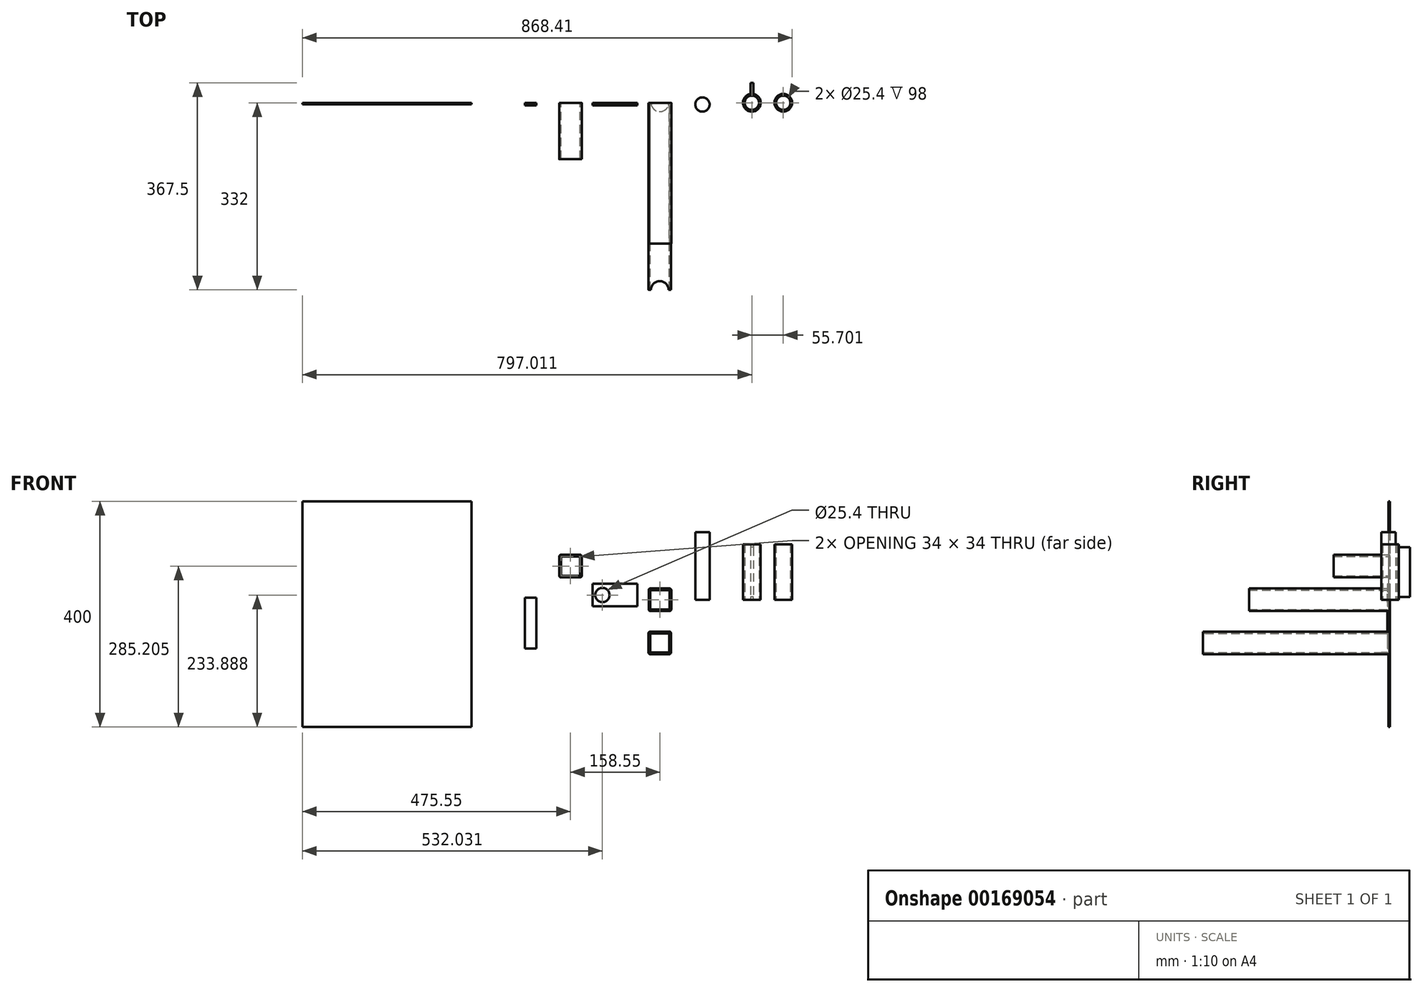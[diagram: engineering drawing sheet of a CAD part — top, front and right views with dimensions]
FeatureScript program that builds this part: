
annotation { "Feature Type Name" : "Feature", "Feature Type Description" : "" }
export const myFeature = defineFeature(function(context is Context, id is Id, definition is map)
    precondition{}
    {
        {
            var Q0;
            Q0=qCreatedBy(makeId("Front.planeOp"),FACE);
            var sketch = newSketch(context, id + "F0", { "sketchPlane" : qUnion([Q0])});
            skLineSegment(sketch, "E0.bottom", {"start": v(17, 20) * mm, "end": v(-17, 20) * mm});
            skLineSegment(sketch, "E0.top", {"start": v(17, -20) * mm, "end": v(-17, -20) * mm});
            skLineSegment(sketch, "E0.left", {"start": v(20, 17) * mm, "end": v(20, -17) * mm});
            skLineSegment(sketch, "E0.right", {"start": v(-20, 17) * mm, "end": v(-20, -17) * mm});
            skPoint(sketch, "E0.middle", {"position": v(0, 0) * mm});
            skLineSegment(sketch, "E1.0", {"start": v(15, 17) * mm, "end": v(-15, 17) * mm});
            skLineSegment(sketch, "E1.1", {"start": v(17, 15) * mm, "end": v(17, -15) * mm});
            skLineSegment(sketch, "E1.2", {"start": v(15, -17) * mm, "end": v(-15, -17) * mm});
            skLineSegment(sketch, "E1.3", {"start": v(-17, 15) * mm, "end": v(-17, -15) * mm});
            skPoint(sketch, "E2.visualSharp", {"position": v(-20, 20) * mm});
            skArc(sketch, "E2.filletArc", {"start": v(-17, 20) * mm, "mid": v(-19.12, 19.12) * mm, "end": v(-20, 17) * mm});
            skPoint(sketch, "E3.visualSharp", {"position": v(20, 20) * mm});
            skArc(sketch, "E3.filletArc", {"start": v(20, 17) * mm, "mid": v(19.12, 19.12) * mm, "end": v(17, 20) * mm});
            skPoint(sketch, "E4.visualSharp", {"position": v(20, -20) * mm});
            skArc(sketch, "E4.filletArc", {"start": v(17, -20) * mm, "mid": v(19.12, -19.12) * mm, "end": v(20, -17) * mm});
            skPoint(sketch, "E5.visualSharp", {"position": v(-20, -20) * mm});
            skArc(sketch, "E5.filletArc", {"start": v(-20, -17) * mm, "mid": v(-19.12, -19.12) * mm, "end": v(-17, -20) * mm});
            skArc(sketch, "E6.filletArc", {"start": v(15, -17) * mm, "mid": v(16.41, -16.41) * mm, "end": v(17, -15) * mm});
            skArc(sketch, "E7.filletArc", {"start": v(17, 15) * mm, "mid": v(16.41, 16.41) * mm, "end": v(15, 17) * mm});
            skArc(sketch, "E8.filletArc", {"start": v(-15, 17) * mm, "mid": v(-16.41, 16.41) * mm, "end": v(-17, 15) * mm});
            skArc(sketch, "E9.filletArc", {"start": v(-17, -15) * mm, "mid": v(-16.41, -16.41) * mm, "end": v(-15, -17) * mm});
            skSolve(sketch);
        }
        {
            var Q0;
            Q0=makeQuery(id+"F0.imprint","IMPRINT",FACE,{"disambiguationData":[TD([[makeQuery(id+"F0.imprint","IMPRINT",EDGE,{"derivedFrom":sQuery(id+"F0.wireOp",EDGE,"E0.bottom")}),1.0]])]});
            extrude(context, id + "F1", {"entities" : qUnion([Q0]), "depth" : 250 * mm});
        }
        {
            var Q0;
            Q0=qCreatedBy(makeId("Front.planeOp"),FACE);
            var sketch = newSketch(context, id + "F2", { "sketchPlane" : qUnion([Q0])});
            skLineSegment(sketch, "E10.bottom", {"start": v(-141.55, 79.68) * mm, "end": v(-175.55, 79.68) * mm});
            skLineSegment(sketch, "E10.top", {"start": v(-141.55, 39.68) * mm, "end": v(-175.55, 39.68) * mm});
            skLineSegment(sketch, "E10.left", {"start": v(-138.55, 76.68) * mm, "end": v(-138.55, 42.68) * mm});
            skLineSegment(sketch, "E10.right", {"start": v(-178.55, 76.68) * mm, "end": v(-178.55, 42.68) * mm});
            skPoint(sketch, "E10.middle", {"position": v(-158.55, 59.68) * mm});
            skLineSegment(sketch, "E11.0", {"start": v(-143.55, 76.68) * mm, "end": v(-173.55, 76.68) * mm});
            skLineSegment(sketch, "E11.1", {"start": v(-141.55, 74.68) * mm, "end": v(-141.55, 44.68) * mm});
            skLineSegment(sketch, "E11.2", {"start": v(-143.55, 42.68) * mm, "end": v(-173.55, 42.68) * mm});
            skLineSegment(sketch, "E11.3", {"start": v(-175.55, 74.68) * mm, "end": v(-175.55, 44.68) * mm});
            skPoint(sketch, "E12.visualSharp", {"position": v(-178.55, 79.68) * mm});
            skArc(sketch, "E12.filletArc", {"start": v(-175.55, 79.68) * mm, "mid": v(-177.67, 78.8) * mm, "end": v(-178.55, 76.68) * mm});
            skPoint(sketch, "E13.visualSharp", {"position": v(-138.55, 79.68) * mm});
            skArc(sketch, "E13.filletArc", {"start": v(-138.55, 76.68) * mm, "mid": v(-139.43, 78.8) * mm, "end": v(-141.55, 79.68) * mm});
            skPoint(sketch, "E14.visualSharp", {"position": v(-138.55, 39.68) * mm});
            skArc(sketch, "E14.filletArc", {"start": v(-141.55, 39.68) * mm, "mid": v(-139.43, 40.56) * mm, "end": v(-138.55, 42.68) * mm});
            skPoint(sketch, "E15.visualSharp", {"position": v(-178.55, 39.68) * mm});
            skArc(sketch, "E15.filletArc", {"start": v(-178.55, 42.68) * mm, "mid": v(-177.67, 40.56) * mm, "end": v(-175.55, 39.68) * mm});
            skArc(sketch, "E16.filletArc", {"start": v(-143.55, 42.68) * mm, "mid": v(-142.14, 43.27) * mm, "end": v(-141.55, 44.68) * mm});
            skArc(sketch, "E17.filletArc", {"start": v(-141.55, 74.68) * mm, "mid": v(-142.14, 76.1) * mm, "end": v(-143.55, 76.68) * mm});
            skArc(sketch, "E18.filletArc", {"start": v(-173.55, 76.68) * mm, "mid": v(-174.96, 76.1) * mm, "end": v(-175.55, 74.68) * mm});
            skArc(sketch, "E19.filletArc", {"start": v(-175.55, 44.68) * mm, "mid": v(-174.96, 43.27) * mm, "end": v(-173.55, 42.68) * mm});
            skSolve(sketch);
        }
        {
            var Q0;
            Q0=makeQuery(id+"F2.imprint","IMPRINT",FACE,{"disambiguationData":[TD([[makeQuery(id+"F2.imprint","IMPRINT",EDGE,{"derivedFrom":sQuery(id+"F2.wireOp",EDGE,"E10.bottom")}),1.0]])]});
            extrude(context, id + "F3", {"entities" : qUnion([Q0]), "depth" : 100 * mm});
        }
        {
            var Q0;
            Q0=qCreatedBy(makeId("Front.planeOp"),FACE);
            var sketch = newSketch(context, id + "F4", { "sketchPlane" : qUnion([Q0])});
            skLineSegment(sketch, "E20.bottom", {"start": v(-119.77, 28.37) * mm, "end": v(-39.77, 28.37) * mm});
            skLineSegment(sketch, "E20.top", {"start": v(-119.77, -11.63) * mm, "end": v(-39.77, -11.63) * mm});
            skLineSegment(sketch, "E20.left", {"start": v(-119.77, 28.37) * mm, "end": v(-119.77, -11.63) * mm});
            skLineSegment(sketch, "E20.right", {"start": v(-39.77, 28.37) * mm, "end": v(-39.77, -11.63) * mm});
            skCircle(sketch, "E21", {"center": v(-102.07, 8.37) * mm, "radius": 12.7 * mm});
            skPoint(sketch, "E21.centerSnap0", {"position": v(-119.77, 8.37) * mm});
            skSolve(sketch);
        }
        {
            var Q0;
            Q0=makeQuery(id+"F4.imprint","IMPRINT",FACE,{"disambiguationData":[TD([[makeQuery(id+"F4.imprint","IMPRINT",EDGE,{"derivedFrom":sQuery(id+"F4.wireOp",EDGE,"E20.bottom")}),-1.0]])]});
            extrude(context, id + "F5", {"entities" : qUnion([Q0]), "depth" : 5 * mm});
        }
        {
            var Q0;
            Q0=qCreatedBy(makeId("Top.planeOp"),FACE);
            var sketch = newSketch(context, id + "F6", { "sketchPlane" : qUnion([Q0])});
            skCircle(sketch, "E22", {"center": v(75.3, -3.08) * mm, "radius": 12.7 * mm});
            skSolve(sketch);
        }
        {
            var Q0;
            Q0 = qSketchRegion(id + "F6", true);
            extrude(context, id + "F7", {"entities" : qUnion([Q0]), "depth" : 120 * mm});
        }
        {
            var Q0;
            Q0=qCreatedBy(makeId("Top.planeOp"),FACE);
            var sketch = newSketch(context, id + "F8", { "sketchPlane" : qUnion([Q0])});
            skCircle(sketch, "E23", {"center": v(162.91, 0) * mm, "radius": 12.7 * mm});
            skCircle(sketch, "E24.0", {"center": v(162.91, 0) * mm, "radius": 15.7 * mm});
            skLineSegment(sketch, "E25", {"start": v(160.41, 15.5) * mm, "end": v(160.41, 35.5) * mm});
            skLineSegment(sketch, "E26", {"start": v(160.41, 35.5) * mm, "end": v(165.41, 35.5) * mm});
            skLineSegment(sketch, "E27", {"start": v(165.41, 35.5) * mm, "end": v(165.41, 15.5) * mm});
            skPoint(sketch, "E28", {"position": v(162.91, 35.5) * mm});
            skSolve(sketch);
        }
        {
            var Q0;
            Q0 = qSketchRegion(id + "F8", true);
            extrude(context, id + "F9", {"entities" : qUnion([Q0]), "depth" : 98 * mm});
        }
        {
            var Q0;
            Q0=qCreatedBy(makeId("Front.planeOp"),FACE);
            var sketch = newSketch(context, id + "F10", { "sketchPlane" : qUnion([Q0])});
            skLineSegment(sketch, "E29.bottom", {"start": v(-239.33, 3.6) * mm, "end": v(-219.33, 3.6) * mm});
            skLineSegment(sketch, "E29.top", {"start": v(-239.33, -86.4) * mm, "end": v(-219.33, -86.4) * mm});
            skLineSegment(sketch, "E29.left", {"start": v(-239.33, 3.6) * mm, "end": v(-239.33, -86.4) * mm});
            skLineSegment(sketch, "E29.right", {"start": v(-219.33, 3.6) * mm, "end": v(-219.33, -86.4) * mm});
            skSolve(sketch);
        }
        {
            var Q0;
            Q0=makeQuery(id+"F10.imprint","IMPRINT",FACE,{"disambiguationData":[TD([[makeQuery(id+"F10.imprint","IMPRINT",EDGE,{"derivedFrom":sQuery(id+"F10.wireOp",EDGE,"E29.bottom")}),-1.0]])]});
            extrude(context, id + "F11", {"entities" : qUnion([Q0]), "depth" : 5 * mm});
        }
        {
            var Q0;
            Q0=qCreatedBy(makeId("Front.planeOp"),FACE);
            var sketch = newSketch(context, id + "F12", { "sketchPlane" : qUnion([Q0])});
            skLineSegment(sketch, "E30.bottom", {"start": v(-634.1, 174.48) * mm, "end": v(-334.1, 174.48) * mm});
            skLineSegment(sketch, "E30.top", {"start": v(-634.1, -225.52) * mm, "end": v(-334.1, -225.52) * mm});
            skLineSegment(sketch, "E30.left", {"start": v(-634.1, 174.48) * mm, "end": v(-634.1, -225.52) * mm});
            skLineSegment(sketch, "E30.right", {"start": v(-334.1, 174.48) * mm, "end": v(-334.1, -225.52) * mm});
            skSolve(sketch);
        }
        {
            var Q0;
            Q0=makeQuery(id+"F12.imprint","IMPRINT",FACE,{"disambiguationData":[TD([[makeQuery(id+"F12.imprint","IMPRINT",EDGE,{"derivedFrom":sQuery(id+"F12.wireOp",EDGE,"E30.bottom")}),-1.0]])]});
            extrude(context, id + "F13", {"entities" : qUnion([Q0]), "depth" : 3 * mm});
        }
        {
            var Q0;
            Q0=makeQuery(id+"F9.opExtrude","SWEPT_FACE",FACE,{"disambiguationData":[OSD([sQuery(id+"F8.wireOp",EDGE,"E25")])]});
            var sketch = newSketch(context, id + "F14", { "sketchPlane" : qUnion([Q0])});
            skLineSegment(sketch, "E31.bottom", {"start": v(-35.5, 0) * mm, "end": v(-15.5, 0) * mm});
            skLineSegment(sketch, "E31.top", {"start": v(-35.5, 5) * mm, "end": v(-15.5, 5) * mm});
            skLineSegment(sketch, "E31.left", {"start": v(-35.5, 0) * mm, "end": v(-35.5, 5) * mm});
            skLineSegment(sketch, "E31.right", {"start": v(-15.5, 0) * mm, "end": v(-15.5, 5) * mm});
            skLineSegment(sketch, "E32.bottom", {"start": v(-35.5, 98) * mm, "end": v(-15.5, 98) * mm});
            skLineSegment(sketch, "E32.top", {"start": v(-35.5, 93) * mm, "end": v(-15.5, 93) * mm});
            skLineSegment(sketch, "E32.left", {"start": v(-35.5, 98) * mm, "end": v(-35.5, 93) * mm});
            skLineSegment(sketch, "E32.right", {"start": v(-15.5, 98) * mm, "end": v(-15.5, 93) * mm});
            skSolve(sketch);
        }
        {
            var Q0;
            Q0 = qSketchRegion(id + "F14", true);
            extrude(context, id + "F15", {"entities" : qUnion([Q0]), "operationType" : NewBodyOperationType.REMOVE, "oppositeDirection" : true, "depth" : 25 * mm});
        }
        {
            var Q0;
            Q0=qCreatedBy(makeId("Top.planeOp"),FACE);
            var sketch = newSketch(context, id + "F16", { "sketchPlane" : qUnion([Q0])});
            skCircle(sketch, "E33", {"center": v(218.61, 0) * mm, "radius": 12.7 * mm});
            skCircle(sketch, "E34.0", {"center": v(218.61, 0) * mm, "radius": 15.7 * mm});
            skSolve(sketch);
        }
        {
            var Q0;
            Q0=makeQuery(id+"F16.imprint","IMPRINT",FACE,{"disambiguationData":[TD([[makeQuery(id+"F16.imprint","IMPRINT",EDGE,{"derivedFrom":sQuery(id+"F16.wireOp",EDGE,"E33")}),-1.0]])]});
            extrude(context, id + "F17", {"entities" : qUnion([Q0]), "depth" : 98 * mm});
        }
        {
            var Q0;
            Q0=qCreatedBy(makeId("Front.planeOp"),FACE);
            var sketch = newSketch(context, id + "F18", { "sketchPlane" : qUnion([Q0])});
            skLineSegment(sketch, "E35.bottom", {"start": v(16.65, -56.52) * mm, "end": v(-17.35, -56.52) * mm});
            skLineSegment(sketch, "E35.top", {"start": v(16.65, -96.52) * mm, "end": v(-17.35, -96.52) * mm});
            skLineSegment(sketch, "E35.left", {"start": v(19.65, -59.52) * mm, "end": v(19.65, -93.52) * mm});
            skLineSegment(sketch, "E35.right", {"start": v(-20.35, -59.52) * mm, "end": v(-20.35, -93.52) * mm});
            skPoint(sketch, "E35.middle", {"position": v(-0.35, -76.52) * mm});
            skLineSegment(sketch, "E36.0", {"start": v(14.65, -59.52) * mm, "end": v(-15.35, -59.52) * mm});
            skLineSegment(sketch, "E36.1", {"start": v(16.65, -61.52) * mm, "end": v(16.65, -91.52) * mm});
            skLineSegment(sketch, "E36.2", {"start": v(14.65, -93.52) * mm, "end": v(-15.35, -93.52) * mm});
            skLineSegment(sketch, "E36.3", {"start": v(-17.35, -61.52) * mm, "end": v(-17.35, -91.52) * mm});
            skPoint(sketch, "E37.visualSharp", {"position": v(-20.35, -56.52) * mm});
            skArc(sketch, "E37.filletArc", {"start": v(-17.35, -56.52) * mm, "mid": v(-19.47, -57.4) * mm, "end": v(-20.35, -59.52) * mm});
            skPoint(sketch, "E38.visualSharp", {"position": v(19.65, -56.52) * mm});
            skArc(sketch, "E38.filletArc", {"start": v(19.65, -59.52) * mm, "mid": v(18.78, -57.4) * mm, "end": v(16.65, -56.52) * mm});
            skPoint(sketch, "E39.visualSharp", {"position": v(19.65, -96.52) * mm});
            skArc(sketch, "E39.filletArc", {"start": v(16.65, -96.52) * mm, "mid": v(18.78, -95.64) * mm, "end": v(19.65, -93.52) * mm});
            skPoint(sketch, "E40.visualSharp", {"position": v(-20.35, -96.52) * mm});
            skArc(sketch, "E40.filletArc", {"start": v(-20.35, -93.52) * mm, "mid": v(-19.47, -95.64) * mm, "end": v(-17.35, -96.52) * mm});
            skArc(sketch, "E41.filletArc", {"start": v(14.65, -93.52) * mm, "mid": v(16.07, -92.94) * mm, "end": v(16.65, -91.52) * mm});
            skArc(sketch, "E42.filletArc", {"start": v(16.65, -61.52) * mm, "mid": v(16.07, -60.1) * mm, "end": v(14.65, -59.52) * mm});
            skArc(sketch, "E43.filletArc", {"start": v(-15.35, -59.52) * mm, "mid": v(-16.76, -60.1) * mm, "end": v(-17.35, -61.52) * mm});
            skArc(sketch, "E44.filletArc", {"start": v(-17.35, -91.52) * mm, "mid": v(-16.76, -92.94) * mm, "end": v(-15.35, -93.52) * mm});
            skSolve(sketch);
        }
        {
            var Q0;
            Q0=makeQuery(id+"F18.imprint","IMPRINT",FACE,{"disambiguationData":[TD([[makeQuery(id+"F18.imprint","IMPRINT",EDGE,{"derivedFrom":sQuery(id+"F18.wireOp",EDGE,"E35.bottom")}),1.0]])]});
            extrude(context, id + "F19", {"entities" : qUnion([Q0]), "depth" : 332 * mm});
        }
        {
            var Q0;
            Q0=makeQuery(id+"F19.opExtrude","SWEPT_FACE",FACE,{"disambiguationData":[OSD([sQuery(id+"F18.wireOp",EDGE,"E35.top")])]});
            var sketch = newSketch(context, id + "F20", { "sketchPlane" : qUnion([Q0])});
            skCircle(sketch, "E45", {"center": v(-0.35, 332) * mm, "radius": 15.7 * mm});
            skCircle(sketch, "E46", {"center": v(0, 0) * mm, "radius": 15.7 * mm});
            skSolve(sketch);
        }
        {
            var Q0;
            Q0 = qSketchRegion(id + "F20", true);
            var Q1;
            {var subQ0=sQuery(id+"F20.wireOp",EDGE,"E45");var subQ1=makeQuery(id+"F19.opExtrude","CAP_EDGE",EDGE,{"disambiguationData":[OSD([sQuery(id+"F18.wireOp",EDGE,"E35.top")])],"isStart":false});var subQ2=makeQuery(id+"F20.imprint","INTERSECT",VERTEX,{"disambiguationData":[OD(0.0)],"derivedFrom":[subQ1,subQ0]});Q1=makeQuery(id+"F20.imprint","IMPRINT",FACE,{"disambiguationData":[TD([[makeQuery(id+"F20.imprint","IMPRINT",EDGE,{"disambiguationData":[TD([[subQ2,-1.0]])],"derivedFrom":subQ0}),1.0]])]});}
            var Q2;
            Q2=makeQuery(id+"F19.opExtrude","SWEPT_FACE",FACE,{"disambiguationData":[OSD([sQuery(id+"F18.wireOp",EDGE,"E35.bottom")])]});
            extrude(context, id + "F21", {"entities" : qUnion([Q0, Q1]), "operationType" : NewBodyOperationType.REMOVE, "endBound" : BoundingType.UP_TO_SURFACE, "oppositeDirection" : true, "endBoundEntityFace" : qUnion([Q2]), "depth" : 25 * mm});
        }
    });
